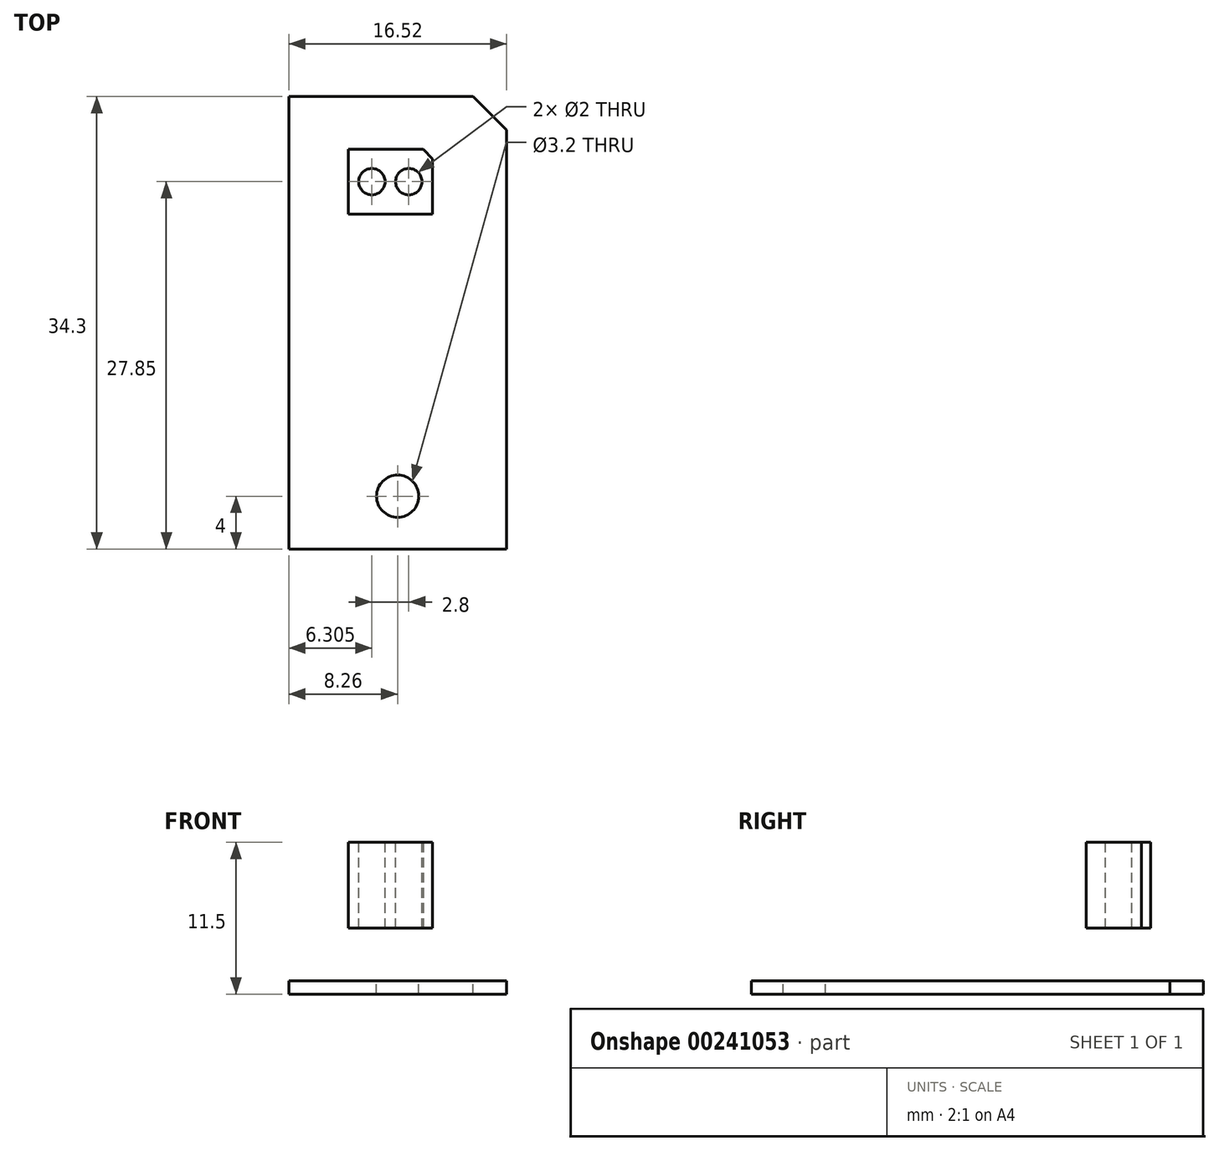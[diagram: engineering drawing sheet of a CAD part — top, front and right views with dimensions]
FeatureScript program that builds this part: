
annotation { "Feature Type Name" : "Feature", "Feature Type Description" : "" }
export const myFeature = defineFeature(function(context is Context, id is Id, definition is map)
    precondition{}
    {
        {
            var Q0;
            Q0=qCreatedBy(makeId("Top.planeOp"),FACE);
            var sketch = newSketch(context, id + "F0", { "sketchPlane" : qUnion([Q0])});
            skLineSegment(sketch, "E0", {"start": v(-8.26, 17.15) * mm, "end": v(-8.25, -17.15) * mm});
            skLineSegment(sketch, "E1", {"start": v(-8.26, -17.15) * mm, "end": v(8.26, -17.15) * mm});
            skLineSegment(sketch, "E2", {"start": v(8.26, -17.15) * mm, "end": v(8.25, 14.61) * mm});
            skLineSegment(sketch, "E3", {"start": v(8.26, 14.61) * mm, "end": v(5.71, 17.15) * mm});
            skLineSegment(sketch, "E4", {"start": v(5.71, 17.15) * mm, "end": v(-8.26, 17.15) * mm});
            skPoint(sketch, "E5", {"position": v(-8.25, 0) * mm});
            skPoint(sketch, "E6", {"position": v(0, -17.15) * mm});
            skSolve(sketch);
        }
        {
            var Q0;
            Q0=makeQuery(id+"F0.imprint","IMPRINT",FACE,{"disambiguationData":[TD([[makeQuery(id+"F0.imprint","IMPRINT",EDGE,{"derivedFrom":sQuery(id+"F0.wireOp",EDGE,"E0")}),1.0]])]});
            extrude(context, id + "F1", {"entities" : qUnion([Q0]), "oppositeDirection" : true, "depth" : 1 * mm});
        }
        {
            var Q0;
            Q0=makeQuery(id+"F1.opExtrude","CAP_FACE",FACE,{"disambiguationData":[OSD([sQuery(id+"F0.wireOp",EDGE,"E0"),sQuery(id+"F0.wireOp",EDGE,"E1"),sQuery(id+"F0.wireOp",EDGE,"E2"),sQuery(id+"F0.wireOp",EDGE,"E3"),sQuery(id+"F0.wireOp",EDGE,"E4")])],"isStart":true});
            var sketch = newSketch(context, id + "F2", { "sketchPlane" : qUnion([Q0])});
            skCircle(sketch, "E7", {"center": v(0, -13.15) * mm, "radius": 1.6 * mm});
            skSolve(sketch);
        }
        {
            var Q0;
            Q0=makeQuery(id+"F2.imprint","IMPRINT",FACE,{"disambiguationData":[TD([[makeQuery(id+"F2.imprint","IMPRINT",EDGE,{"derivedFrom":sQuery(id+"F2.wireOp",EDGE,"E7")}),1.0]])]});
            var Q1;
            Q1=makeQuery(id+"F1.opExtrude","CAP_FACE",FACE,{"disambiguationData":[OSD([sQuery(id+"F0.wireOp",EDGE,"E0"),sQuery(id+"F0.wireOp",EDGE,"E1"),sQuery(id+"F0.wireOp",EDGE,"E2"),sQuery(id+"F0.wireOp",EDGE,"E3"),sQuery(id+"F0.wireOp",EDGE,"E4")])],"isStart":false});
            extrude(context, id + "F3", {"entities" : qUnion([Q0]), "operationType" : NewBodyOperationType.REMOVE, "endBound" : BoundingType.UP_TO_SURFACE, "oppositeDirection" : true, "endBoundEntityFace" : qUnion([Q1]), "depth" : 25 * mm});
        }
        {
            var Q0;
            Q0=qCreatedBy(makeId("Top.planeOp"),FACE);
            cPlane(context, id + "F4", {"entities" : qUnion([Q0]), "cplaneType" : CPlaneType.OFFSET, "offset" : 4 * mm, "width" : 150 * mm, "height" : 150 * mm});
        }
        {
            var Q0;
            Q0=qCreatedBy(id+"F4.planeOp",FACE);
            var sketch = newSketch(context, id + "F5", { "sketchPlane" : qUnion([Q0])});
            skLineSegment(sketch, "E8.0.0", {"start": v(8.26, 14.61) * mm, "end": v(5.71, 17.15) * mm});
            skLineSegment(sketch, "E8.0.1", {"start": v(5.71, 17.15) * mm, "end": v(-8.26, 17.15) * mm});
            skLineSegment(sketch, "E8.0.2", {"start": v(-8.26, 17.15) * mm, "end": v(-8.25, -17.15) * mm});
            skLineSegment(sketch, "E8.0.3", {"start": v(-8.25, -17.15) * mm, "end": v(8.26, -17.15) * mm});
            skLineSegment(sketch, "E8.0.4", {"start": v(8.26, -17.15) * mm, "end": v(8.25, 14.61) * mm});
            skLineSegment(sketch, "E9", {"start": v(-3.76, 13.15) * mm, "end": v(-3.75, 8.25) * mm});
            skLineSegment(sketch, "E10", {"start": v(-3.75, 8.25) * mm, "end": v(2.64, 8.25) * mm});
            skLineSegment(sketch, "E11", {"start": v(2.64, 8.25) * mm, "end": v(2.64, 12.44) * mm});
            skLineSegment(sketch, "E12", {"start": v(2.65, 12.44) * mm, "end": v(1.94, 13.15) * mm});
            skLineSegment(sketch, "E13", {"start": v(1.94, 13.15) * mm, "end": v(-3.76, 13.15) * mm});
            skSolve(sketch);
        }
        {
            var Q0;
            Q0=makeQuery(id+"F5.imprint","IMPRINT",FACE,{"disambiguationData":[TD([[makeQuery(id+"F5.imprint","IMPRINT",EDGE,{"derivedFrom":sQuery(id+"F5.wireOp",EDGE,"E9")}),1.0]])]});
            extrude(context, id + "F6", {"entities" : qUnion([Q0]), "depth" : 6.5 * mm});
        }
        {
            var Q0;
            Q0=makeQuery(id+"F6.opExtrude","CAP_FACE",FACE,{"disambiguationData":[OSD([sQuery(id+"F5.wireOp",EDGE,"E9"),sQuery(id+"F5.wireOp",EDGE,"E10"),sQuery(id+"F5.wireOp",EDGE,"E11"),sQuery(id+"F5.wireOp",EDGE,"E12"),sQuery(id+"F5.wireOp",EDGE,"E13")])],"isStart":false});
            var sketch = newSketch(context, id + "F7", { "sketchPlane" : qUnion([Q0])});
            skCircle(sketch, "E14", {"center": v(-1.96, 10.7) * mm, "radius": 1 * mm});
            skCircle(sketch, "E15", {"center": v(0.84, 10.7) * mm, "radius": 1 * mm});
            skLineSegment(sketch, "E16", {"start": v(-1.96, 10.7) * mm, "end": v(0.84, 10.7) * mm, "construction": true});
            skPoint(sketch, "E17", {"position": v(-0.56, 10.7) * mm});
            skPoint(sketch, "E18", {"position": v(-0.55, 8.25) * mm});
            skPoint(sketch, "E19", {"position": v(-3.76, 10.7) * mm});
            skSolve(sketch);
        }
        {
            var Q0;
            Q0=makeQuery(id+"F7.imprint","IMPRINT",FACE,{"disambiguationData":[TD([[makeQuery(id+"F7.imprint","IMPRINT",EDGE,{"derivedFrom":sQuery(id+"F7.wireOp",EDGE,"E14")}),1.0]])]});
            var Q1;
            Q1=makeQuery(id+"F7.imprint","IMPRINT",FACE,{"disambiguationData":[TD([[makeQuery(id+"F7.imprint","IMPRINT",EDGE,{"derivedFrom":sQuery(id+"F7.wireOp",EDGE,"E15")}),1.0]])]});
            var Q2;
            Q2=makeQuery(id+"F6.opExtrude","CAP_FACE",FACE,{"disambiguationData":[OSD([sQuery(id+"F5.wireOp",EDGE,"E9"),sQuery(id+"F5.wireOp",EDGE,"E10"),sQuery(id+"F5.wireOp",EDGE,"E11"),sQuery(id+"F5.wireOp",EDGE,"E12"),sQuery(id+"F5.wireOp",EDGE,"E13")])],"isStart":true});
            extrude(context, id + "F8", {"entities" : qUnion([Q0, Q1]), "operationType" : NewBodyOperationType.REMOVE, "endBound" : BoundingType.UP_TO_SURFACE, "oppositeDirection" : true, "endBoundEntityFace" : qUnion([Q2]), "depth" : 25 * mm});
        }
    });
